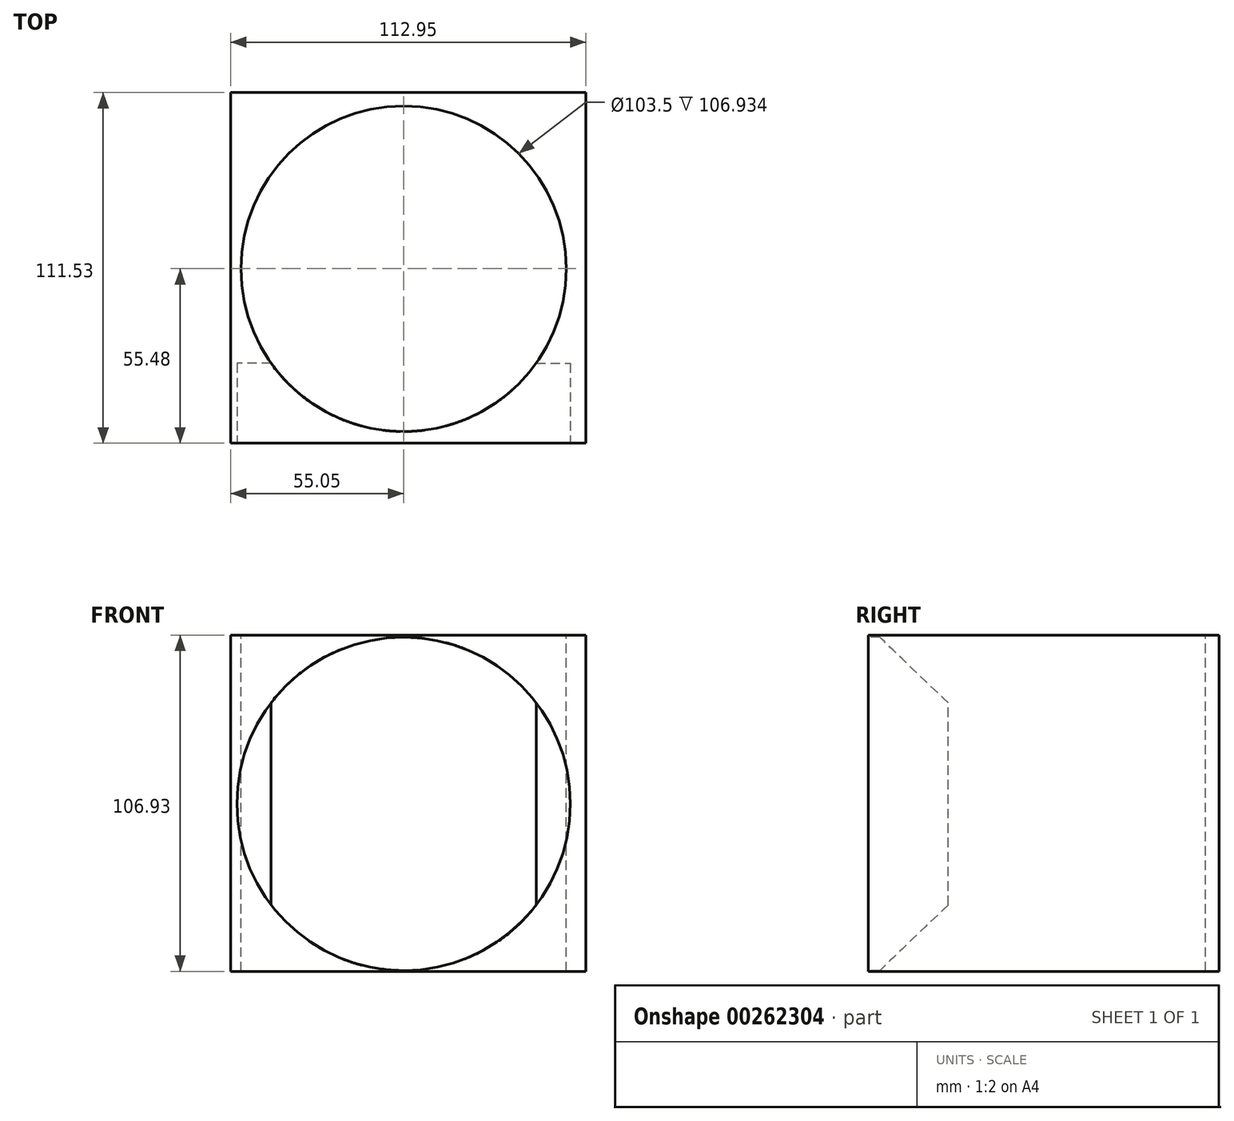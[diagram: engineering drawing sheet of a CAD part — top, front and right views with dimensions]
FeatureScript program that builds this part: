
annotation { "Feature Type Name" : "Feature", "Feature Type Description" : "" }
export const myFeature = defineFeature(function(context is Context, id is Id, definition is map)
    precondition{}
    {
        {
            var Q0;
            Q0=qCreatedBy(makeId("Top.planeOp"),FACE);
            var sketch = newSketch(context, id + "F0", { "sketchPlane" : qUnion([Q0])});
            skLineSegment(sketch, "E0.bottom", {"start": v(-55.05, 56.05) * mm, "end": v(57.9, 56.05) * mm});
            skLineSegment(sketch, "E0.top", {"start": v(-55.05, -55.48) * mm, "end": v(57.9, -55.48) * mm});
            skLineSegment(sketch, "E0.left", {"start": v(-55.05, 56.05) * mm, "end": v(-55.05, -55.48) * mm});
            skLineSegment(sketch, "E0.right", {"start": v(57.9, 56.05) * mm, "end": v(57.9, -55.48) * mm});
            skSolve(sketch);
        }
        {
            var Q0;
            Q0=makeQuery(id+"F0.imprint","IMPRINT",FACE,{"disambiguationData":[TD([[makeQuery(id+"F0.imprint","IMPRINT",EDGE,{"derivedFrom":sQuery(id+"F0.wireOp",EDGE,"E0.bottom")}),-1.0]])]});
            extrude(context, id + "F1", {"entities" : qUnion([Q0]), "depth" : 93.47 * mm});
        }
        {
            var Q0;
            Q0=makeQuery(id+"F1.opExtrude","CAP_FACE",FACE,{"disambiguationData":[OSD([sQuery(id+"F0.wireOp",EDGE,"E0.bottom"),sQuery(id+"F0.wireOp",EDGE,"E0.top"),sQuery(id+"F0.wireOp",EDGE,"E0.left"),sQuery(id+"F0.wireOp",EDGE,"E0.right")])],"isStart":false});
            var sketch = newSketch(context, id + "F2", { "sketchPlane" : qUnion([Q0])});
            skSolve(sketch);
        }
        {
            var Q0;
            Q0 = qSketchRegion(id + "F2", true);
            var Q1;
            Q1=makeQuery(id+"F2.imprint","IMPRINT",FACE,{"disambiguationData":[TD([[makeQuery(id+"F2.imprint","IMPRINT",EDGE,{"derivedFrom":makeQuery(id+"F1.opExtrude","CAP_EDGE",EDGE,{"disambiguationData":[OSD([sQuery(id+"F0.wireOp",EDGE,"E0.bottom")])],"isStart":false})}),-1.0]])]});
            extrude(context, id + "F3", {"entities" : qUnion([Q0, Q1]), "operationType" : NewBodyOperationType.ADD, "depth" : 13.46 * mm});
        }
        {
            var Q0;
            Q0=makeQuery(id+"F3.opExtrude","CAP_FACE",FACE,{"disambiguationData":[OSD([sQuery(id+"F0.wireOp",EDGE,"E0.bottom"),sQuery(id+"F0.wireOp",EDGE,"E0.top"),sQuery(id+"F0.wireOp",EDGE,"E0.left"),sQuery(id+"F0.wireOp",EDGE,"E0.right")])],"isStart":false});
            var sketch = newSketch(context, id + "F4", { "sketchPlane" : qUnion([Q0])});
            skCircle(sketch, "E1", {"center": v(0, 0) * mm, "radius": 51.75 * mm});
            skSolve(sketch);
        }
        {
            var Q0;
            Q0=makeQuery(id+"F4.imprint","IMPRINT",FACE,{"disambiguationData":[TD([[makeQuery(id+"F4.imprint","IMPRINT",EDGE,{"derivedFrom":sQuery(id+"F4.wireOp",EDGE,"E1")}),1.0]])]});
            extrude(context, id + "F5", {"entities" : qUnion([Q0]), "operationType" : NewBodyOperationType.REMOVE, "oppositeDirection" : true, "depth" : 131.32 * mm});
        }
        {
            var Q0;
            {var subQ0=sQuery(id+"F0.wireOp",EDGE,"E0.top");Q0=makeQuery(id+"F3.boolean.opBoolean","MERGE",FACE,{"derivedFrom":[makeQuery(id+"F1.opExtrude","SWEPT_FACE",FACE,{"disambiguationData":[OSD([subQ0])]}),makeQuery(id+"F3.opExtrude","SWEPT_FACE",FACE,{"disambiguationData":[OSD([subQ0])]})]});}
            var sketch = newSketch(context, id + "F6", { "sketchPlane" : qUnion([Q0])});
            skCircle(sketch, "E2", {"center": v(0, 53.24) * mm, "radius": 53 * mm});
            skSolve(sketch);
        }
        {
            var Q0;
            Q0=makeQuery(id+"F6.imprint","IMPRINT",FACE,{"disambiguationData":[TD([[makeQuery(id+"F6.imprint","IMPRINT",EDGE,{"derivedFrom":sQuery(id+"F6.wireOp",EDGE,"E2")}),1.0]])]});
            extrude(context, id + "F7", {"entities" : qUnion([Q0]), "operationType" : NewBodyOperationType.REMOVE, "oppositeDirection" : true, "depth" : 25.4 * mm});
        }
    });
